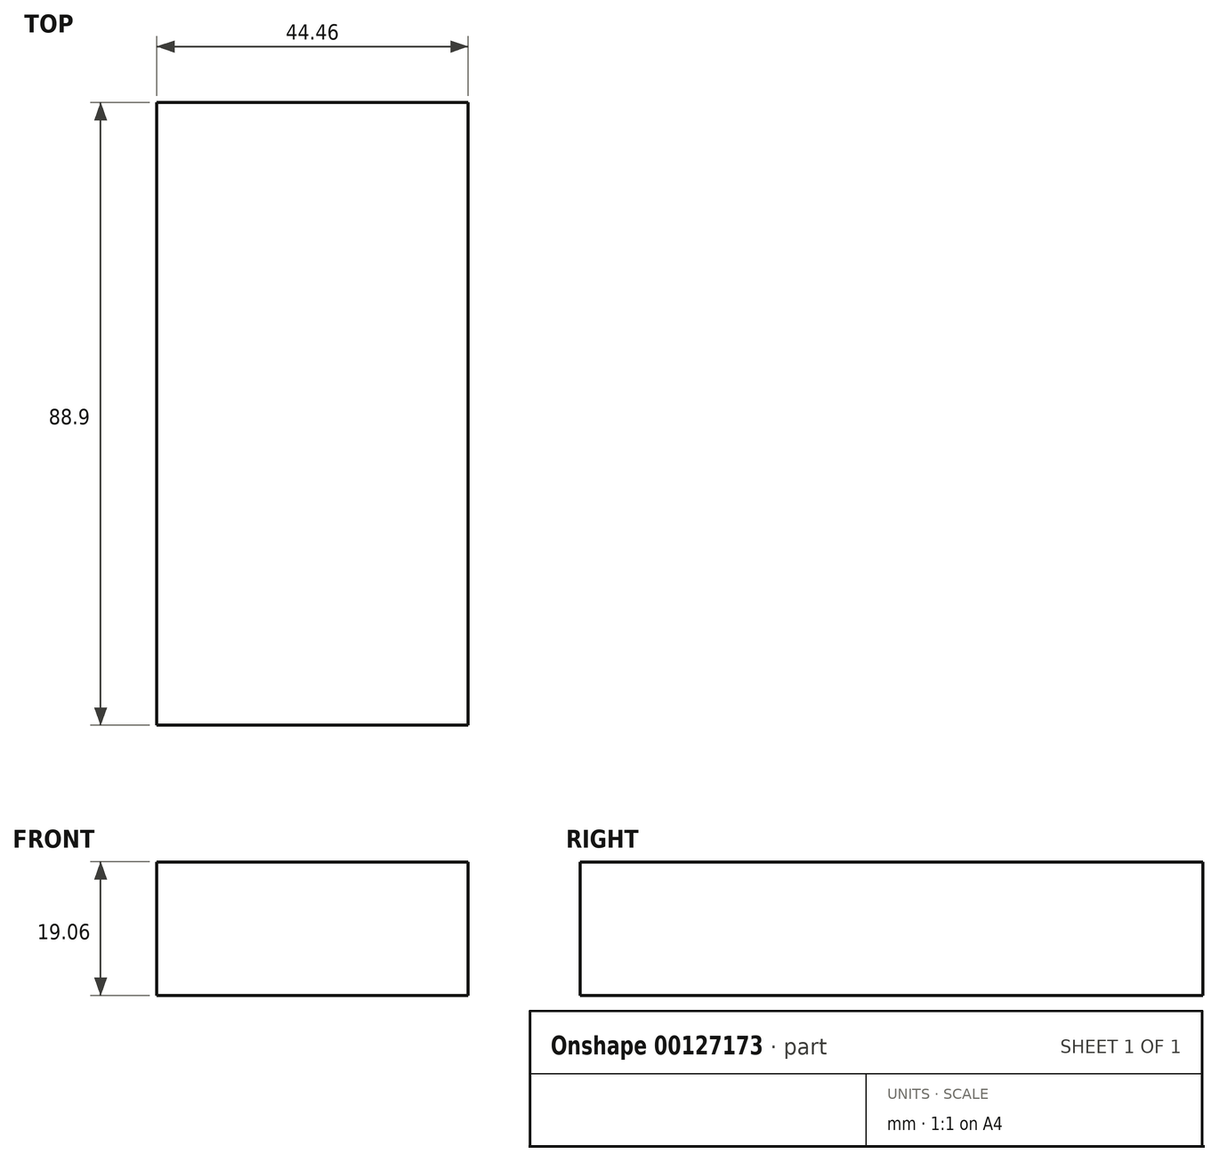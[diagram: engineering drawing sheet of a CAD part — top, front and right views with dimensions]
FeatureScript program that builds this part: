
annotation { "Feature Type Name" : "Feature", "Feature Type Description" : "" }
export const myFeature = defineFeature(function(context is Context, id is Id, definition is map)
    precondition{}
    {
        {
            var Q0;
            Q0=qCreatedBy(makeId("Front.planeOp"),FACE);
            var sketch = newSketch(context, id + "F0", { "sketchPlane" : qUnion([Q0])});
            skLineSegment(sketch, "E0.bottom", {"start": v(22.23, -9.52) * mm, "end": v(-22.23, -9.52) * mm});
            skLineSegment(sketch, "E0.top", {"start": v(22.23, 9.53) * mm, "end": v(-22.23, 9.53) * mm});
            skLineSegment(sketch, "E0.left", {"start": v(22.23, -9.52) * mm, "end": v(22.23, 9.53) * mm});
            skLineSegment(sketch, "E0.right", {"start": v(-22.23, -9.52) * mm, "end": v(-22.23, 9.53) * mm});
            skPoint(sketch, "E0.middle", {"position": v(0, 0) * mm});
            skSolve(sketch);
        }
        {
            var Q0;
            Q0=qSketchRegion(id+"F0",true);
            extrude(context, id + "F1", {"entities" : qUnion([Q0]), "depth" : 88.9 * mm});
        }
    });
